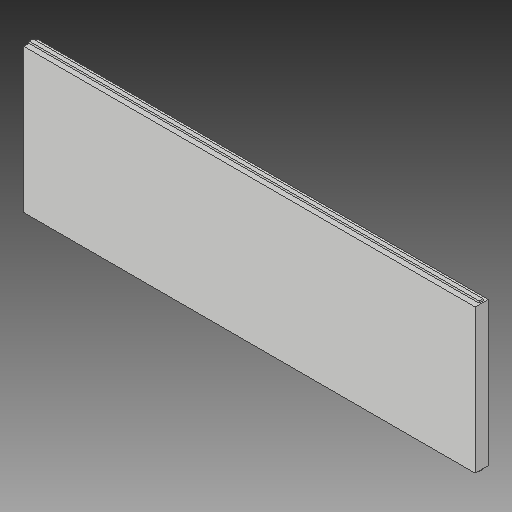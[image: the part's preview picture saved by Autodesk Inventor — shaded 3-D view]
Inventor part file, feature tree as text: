
AUTODESK INVENTOR PART (.ipt)
format: ipt  version: 2018.3 (Build 223284000, 284)  size: 243,712 bytes
history: native  units: mm
features: extrude x4, sketch x4
ambient origin geometry x8: Origin, YZ Plane, XZ Plane, XY Plane, X Axis, Y Axis, Z Axis, Center Point
bodies: Solid1 (feature_tree)
feature tree (8):
  extrude  "Extrusion1"  Depth=11.0mm
  extrude  "Extrusion2"  Depth=0.3mm
  extrude  "Extrusion3"  Depth=0.4mm
  extrude  "Extrusion4"  Depth=34.5mm TaperAngle=0.0deg
  sketch  "Sketch1"  dims[d0=34.5mm d1=11.0mm]
  sketch  "Sketch2"  dims[d2=1.0mm d3=0.0mm d4=0.3mm]
  sketch  "Sketch3"  dims[d5=0.15mm d6=0.4mm]
  sketch  "Sketch4"  dims[d7=0.15mm d8=34.5mm d9=0.0mm d10=0.1mm d11=0.15mm d12=0.0mm d13=0.1mm d14=0.15mm d15=0.0mm]
